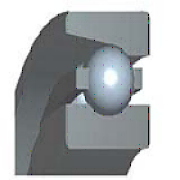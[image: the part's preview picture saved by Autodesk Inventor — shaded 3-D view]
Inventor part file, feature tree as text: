
AUTODESK INVENTOR PART (.ipt)
format: ipt  version: 2018.1 (Build 221171000, 171)  size: 417,792 bytes
history: native  units: mm
features: revolve x2, sketch x1, pattern_circular x1
ambient origin geometry x8: Origin, YZ Plane, XZ Plane, XY Plane, X Axis, Y Axis, Z Axis, Center Point
bodies: Solid1 (feature_tree)
feature tree (4):
  sketch  "Sketch1"  dims[d0=5.0mm d1=1.777778mm d2=13.0mm d3=4.0mm d4=1.333333mm d5=2.094395mm d6=0.4mm d7=0.2mm d8=45.0deg d9=0.133333mm d10=0.133333mm d11=0.133333mm d12=0.133333mm d13=0.133333mm d14=0.133333mm d15=0.133333mm d16=90.0deg d17=0.666667mm d18=2.311111mm d19=90.0deg d20=113.097336mm d21=360.0deg d23=0.0mm d24=0.0mm d25=0.0mm d26=0.0mm d27=0.0mm]
  revolve  "Revolution1"  [1 undecoded]
  revolve  "Revolution2"  [1 undecoded]
  pattern_circular  "Circular Pattern1"  [2 undecoded]
note: 4 required parameter values undecoded (feature->parameter linkage not recoverable at this tier; creation-order binding heuristic only, values carry confidence <= 0.55)